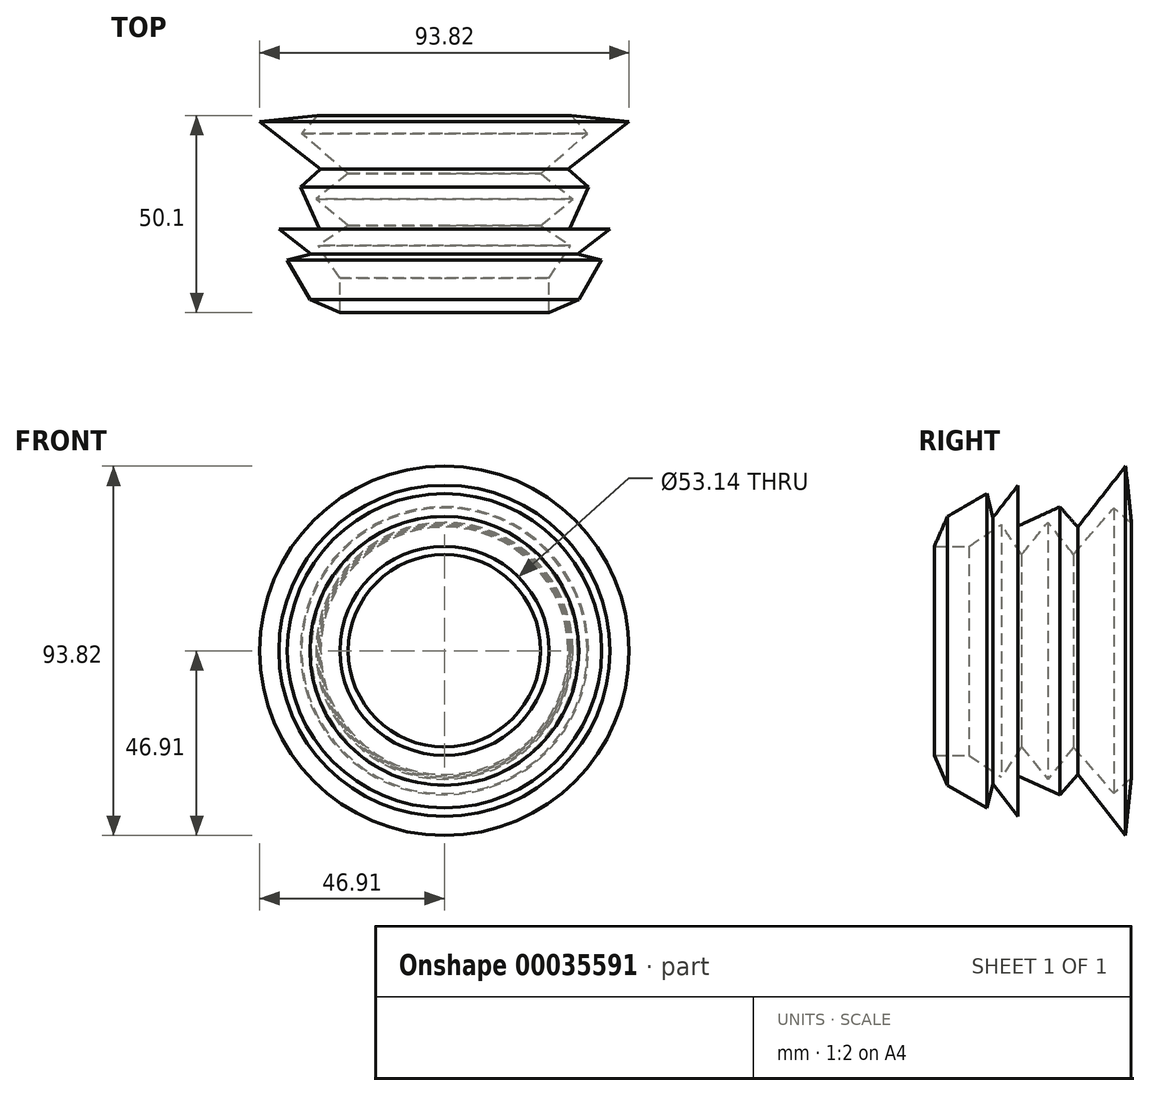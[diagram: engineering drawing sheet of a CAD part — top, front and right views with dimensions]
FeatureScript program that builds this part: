
annotation { "Feature Type Name" : "Feature", "Feature Type Description" : "" }
export const myFeature = defineFeature(function(context is Context, id is Id, definition is map)
    precondition{}
    {
        {
            var Q0;
            Q0=qCreatedBy(makeId("Right.planeOp"),FACE);
            var sketch = newSketch(context, id + "F0", { "sketchPlane" : qUnion([Q0])});
            skLineSegment(sketch, "E0", {"start": v(0, 0) * mm, "end": v(-49.5, 0) * mm});
            skLineSegment(sketch, "E1", {"start": v(-46.76, 34.16) * mm, "end": v(-36.74, 39.93) * mm});
            skLineSegment(sketch, "E2", {"start": v(-36.74, 39.93) * mm, "end": v(-35.22, 33.86) * mm});
            skLineSegment(sketch, "E3", {"start": v(-35.22, 33.86) * mm, "end": v(-28.85, 42.05) * mm});
            skLineSegment(sketch, "E4", {"start": v(-28.85, 42.05) * mm, "end": v(-28.85, 31.73) * mm});
            skLineSegment(sketch, "E5", {"start": v(-28.85, 31.73) * mm, "end": v(-18.22, 36.59) * mm});
            skLineSegment(sketch, "E6", {"start": v(-18.22, 36.59) * mm, "end": v(-13.66, 31.43) * mm});
            skLineSegment(sketch, "E7", {"start": v(-13.66, 31.43) * mm, "end": v(-1.52, 46.91) * mm});
            skLineSegment(sketch, "E8", {"start": v(-1.52, 46.91) * mm, "end": v(0, 32.34) * mm});
            skLineSegment(sketch, "E9", {"start": v(0, 32.34) * mm, "end": v(-4.55, 36.29) * mm});
            skLineSegment(sketch, "E10", {"start": v(-4.55, 36.29) * mm, "end": v(-14.75, 24.52) * mm});
            skLineSegment(sketch, "E11", {"start": v(-14.75, 24.52) * mm, "end": v(-21.26, 32.64) * mm});
            skLineSegment(sketch, "E12", {"start": v(-21.26, 32.64) * mm, "end": v(-27.94, 24.44) * mm});
            skLineSegment(sketch, "E13", {"start": v(-27.94, 24.44) * mm, "end": v(-33.1, 32.03) * mm});
            skLineSegment(sketch, "E14", {"start": v(-33.1, 32.03) * mm, "end": v(-41.3, 26.57) * mm});
            skLineSegment(sketch, "E15", {"start": v(-41.3, 26.57) * mm, "end": v(-50.1, 26.57) * mm});
            skLineSegment(sketch, "E16", {"start": v(-50.1, 26.57) * mm, "end": v(-46.76, 34.16) * mm});
            skSolve(sketch);
        }
        {
            var Q0;
            Q0 = qSketchRegion(id + "F0", true);
            var Q1;
            Q1=sQuery(id+"F0.wireOp",EDGE,"E0");
            revolve(context, id + "F1", {"entities" : qUnion([Q0]), "axis" : qUnion([Q1]), "revolveType" : RevolveType.FULL});
        }
    });
